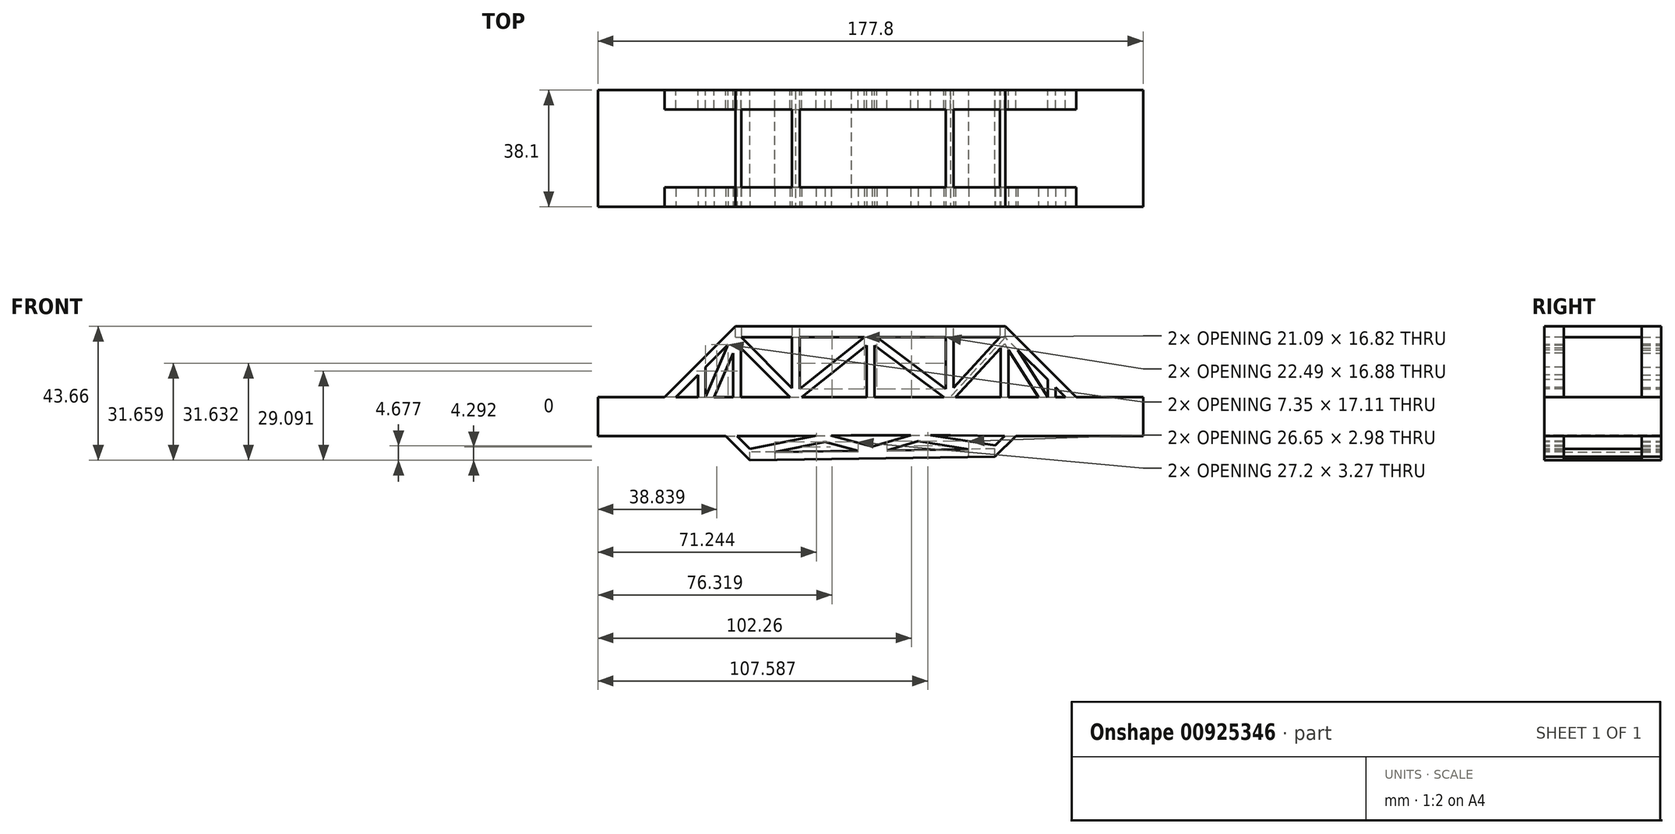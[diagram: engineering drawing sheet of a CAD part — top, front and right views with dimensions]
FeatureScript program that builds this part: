
annotation { "Feature Type Name" : "Feature", "Feature Type Description" : "" }
export const myFeature = defineFeature(function(context is Context, id is Id, definition is map)
    precondition{}
    {
        {
            var Q0;
            Q0=qCreatedBy(makeId("Front.planeOp"),FACE);
            var sketch = newSketch(context, id + "F0", { "sketchPlane" : qUnion([Q0])});
            skLineSegment(sketch, "E0.bottom", {"start": v(-75.3, -1.44) * mm, "end": v(51.7, -1.44) * mm});
            skLineSegment(sketch, "E1.bottom", {"start": v(-75.3, -1.44) * mm, "end": v(-100.7, -1.44) * mm});
            skLineSegment(sketch, "E1.top", {"start": v(-75.3, -14.14) * mm, "end": v(-100.7, -14.14) * mm});
            skLineSegment(sketch, "E1.left", {"start": v(-75.3, -8.45) * mm, "end": v(-75.3, -14.14) * mm});
            skLineSegment(sketch, "E1.right", {"start": v(-100.7, -1.44) * mm, "end": v(-100.7, -14.14) * mm});
            skPoint(sketch, "E2.oppositeSnap0", {"position": v(-88, -14.14) * mm});
            skLineSegment(sketch, "E2.bottom", {"start": v(51.7, -1.44) * mm, "end": v(77.1, -1.44) * mm});
            skLineSegment(sketch, "E2.left", {"start": v(51.7, -1.44) * mm, "end": v(51.7, -13.25) * mm});
            skLineSegment(sketch, "E2.right", {"start": v(77.1, -1.44) * mm, "end": v(77.1, -14.14) * mm});
            skPoint(sketch, "E3", {"position": v(-3.25, -27.46) * mm});
            skPoint(sketch, "E4", {"position": v(-50.06, -19.42) * mm});
            skPoint(sketch, "E5", {"position": v(27.7, -18.29) * mm});
            skPoint(sketch, "E6", {"position": v(-11.78, -13.8) * mm});
            skPoint(sketch, "E7", {"position": v(-36.3, -14.14) * mm});
            skPoint(sketch, "E8", {"position": v(37.87, -8.17) * mm});
            skLineSegment(sketch, "E9", {"start": v(-36.3, -14.14) * mm, "end": v(-36.3, -1.44) * mm});
            skLineSegment(sketch, "E10", {"start": v(-11.78, -13.8) * mm, "end": v(-11.78, -1.44) * mm});
            skLineSegment(sketch, "E11", {"start": v(-75.3, -1.44) * mm, "end": v(-75.3, -1.44) * mm});
            skLineSegment(sketch, "E12", {"start": v(-75.3, -8.45) * mm, "end": v(-75.3, -1.44) * mm});
            skLineSegment(sketch, "E13", {"start": v(51.7, -1.44) * mm, "end": v(32.16, 18.1) * mm});
            skLineSegment(sketch, "E14", {"start": v(32.16, 18.1) * mm, "end": v(-55.77, 18.1) * mm});
            skLineSegment(sketch, "E15", {"start": v(-55.77, 18.1) * mm, "end": v(-75.3, -1.44) * mm});
            skLineSegment(sketch, "E16", {"start": v(-65.53, 8.33) * mm, "end": v(-65.53, -1.44) * mm});
            skLineSegment(sketch, "E17", {"start": v(-64.15, -1.44) * mm, "end": v(-55.77, 18.1) * mm});
            skLineSegment(sketch, "E18", {"start": v(46.02, 4.24) * mm, "end": v(46.02, -1.44) * mm});
            skLineSegment(sketch, "E19", {"start": v(32.16, 18.1) * mm, "end": v(14.23, -1.44) * mm});
            skLineSegment(sketch, "E20", {"start": v(-11.8, 18.1) * mm, "end": v(14.23, -1.44) * mm});
            skLineSegment(sketch, "E21", {"start": v(-36.3, -1.44) * mm, "end": v(-11.8, 18.1) * mm});
            skLineSegment(sketch, "E22", {"start": v(-55.77, 18.1) * mm, "end": v(-36.3, -1.44) * mm});
            skLineSegment(sketch, "E23.1", {"start": v(31.98, 16.02) * mm, "end": v(15.96, -1.44) * mm});
            skLineSegment(sketch, "E23.2", {"start": v(-62.77, -1.44) * mm, "end": v(-55.34, 15.87) * mm});
            skLineSegment(sketch, "E23.3", {"start": v(-55.34, 15.87) * mm, "end": v(-38.08, -1.44) * mm});
            skLineSegment(sketch, "E23.4", {"start": v(-34.25, -1.44) * mm, "end": v(-11.78, 16.5) * mm});
            skLineSegment(sketch, "E23.5", {"start": v(-11.78, 16.5) * mm, "end": v(12.12, -1.44) * mm});
            skLineSegment(sketch, "E24.0", {"start": v(30.44, 18.1) * mm, "end": v(14.07, 0.27) * mm});
            skLineSegment(sketch, "E24.1", {"start": v(-9.69, 18.1) * mm, "end": v(14.07, 0.27) * mm});
            skLineSegment(sketch, "E24.2", {"start": v(-36.2, 0.27) * mm, "end": v(-13.84, 18.1) * mm});
            skLineSegment(sketch, "E24.3", {"start": v(-53.97, 18.1) * mm, "end": v(-36.2, 0.27) * mm});
            skLineSegment(sketch, "E25.0", {"start": v(-55.77, 21.7) * mm, "end": v(-78.9, -1.44) * mm});
            skLineSegment(sketch, "E26", {"start": v(-55.77, 21.7) * mm, "end": v(32.16, 21.7) * mm});
            skLineSegment(sketch, "E27.0", {"start": v(55.3, -1.44) * mm, "end": v(32.16, 21.7) * mm});
            skLineSegment(sketch, "E28", {"start": v(-55.34, -1.44) * mm, "end": v(-55.34, 15.87) * mm});
            skLineSegment(sketch, "E29", {"start": v(31.98, 16.02) * mm, "end": v(31.98, -1.44) * mm});
            skLineSegment(sketch, "E30", {"start": v(-11.78, 16.5) * mm, "end": v(-11.78, -1.44) * mm});
            skLineSegment(sketch, "E31", {"start": v(-36.2, 0.27) * mm, "end": v(-36.2, 18.1) * mm});
            skLineSegment(sketch, "E32", {"start": v(14.07, 0.27) * mm, "end": v(14.07, 18.1) * mm});
            skLineSegment(sketch, "E33.0", {"start": v(-34.92, 1.28) * mm, "end": v(-34.92, 18.1) * mm});
            skLineSegment(sketch, "E34.0", {"start": v(-37.46, 1.54) * mm, "end": v(-37.46, 18.1) * mm});
            skLineSegment(sketch, "E35.0", {"start": v(15.34, 1.65) * mm, "end": v(15.34, 18.1) * mm});
            skLineSegment(sketch, "E36.0", {"start": v(12.8, 1.22) * mm, "end": v(12.8, 18.1) * mm});
            skLineSegment(sketch, "E37.0", {"start": v(-54.07, -1.44) * mm, "end": v(-54.07, 14.6) * mm});
            skLineSegment(sketch, "E38.0", {"start": v(-56.61, -1.44) * mm, "end": v(-56.61, 12.91) * mm});
            skLineSegment(sketch, "E39.0", {"start": v(30.7, 14.63) * mm, "end": v(30.7, -1.44) * mm});
            skLineSegment(sketch, "E40.0", {"start": v(33.25, 14.01) * mm, "end": v(33.25, -1.44) * mm});
            skLineSegment(sketch, "E41", {"start": v(-37.46, 18.1) * mm, "end": v(-34.92, 18.1) * mm});
            skLineSegment(sketch, "E42", {"start": v(-37.46, 1.54) * mm, "end": v(-36.2, 0.27) * mm});
            skLineSegment(sketch, "E43", {"start": v(-36.2, 0.27) * mm, "end": v(-34.92, 1.28) * mm});
            skLineSegment(sketch, "E44.0", {"start": v(-13.05, 15.48) * mm, "end": v(-13.05, -1.44) * mm});
            skLineSegment(sketch, "E45.0", {"start": v(-10.5, 15.54) * mm, "end": v(-10.5, -1.44) * mm});
            skLineSegment(sketch, "E46.0", {"start": v(-68.07, 5.8) * mm, "end": v(-68.07, -1.44) * mm});
            skLineSegment(sketch, "E47", {"start": v(-18.13, -13.87) * mm, "end": v(-18.13, -1.44) * mm});
            skLineSegment(sketch, "E48", {"start": v(-5.43, -13.87) * mm, "end": v(-5.43, -1.44) * mm});
            skLineSegment(sketch, "E49.0", {"start": v(-65.53, -1.44) * mm, "end": v(-58.19, 15.68) * mm});
            skLineSegment(sketch, "E50", {"start": v(-55.34, -1.44) * mm, "end": v(-55.34, -14.14) * mm});
            skLineSegment(sketch, "E51", {"start": v(14.23, -1.44) * mm, "end": v(14.23, -13.87) * mm});
            skLineSegment(sketch, "E52", {"start": v(31.98, -1.44) * mm, "end": v(31.98, -14.14) * mm});
            skLineSegment(sketch, "E53", {"start": v(31.98, -14.14) * mm, "end": v(27.7, -18.29) * mm});
            skLineSegment(sketch, "E54", {"start": v(-50.06, -19.42) * mm, "end": v(27.7, -18.29) * mm});
            skLineSegment(sketch, "E55", {"start": v(-55.34, -14.14) * mm, "end": v(-50.06, -19.42) * mm});
            skPoint(sketch, "E56", {"position": v(3.63, -14.5) * mm});
            skPoint(sketch, "E57", {"position": v(-26.6, -14.74) * mm});
            skLineSegment(sketch, "E58", {"start": v(-75.3, -14.14) * mm, "end": v(-36.3, -14.14) * mm});
            skLineSegment(sketch, "E59", {"start": v(31.98, -14.14) * mm, "end": v(77.1, -14.14) * mm});
            skLineSegment(sketch, "E60.0", {"start": v(35.62, -14.14) * mm, "end": v(28.75, -20.81) * mm});
            skLineSegment(sketch, "E60.1", {"start": v(-51.1, -21.97) * mm, "end": v(28.75, -20.81) * mm});
            skLineSegment(sketch, "E60.2", {"start": v(-58.93, -14.14) * mm, "end": v(-51.1, -21.97) * mm});
            skLineSegment(sketch, "E61", {"start": v(27.7, -18.29) * mm, "end": v(3.63, -14.5) * mm});
            skLineSegment(sketch, "E62", {"start": v(3.63, -14.5) * mm, "end": v(-11.18, -18.85) * mm});
            skLineSegment(sketch, "E63", {"start": v(-11.18, -18.85) * mm, "end": v(-26.6, -14.74) * mm});
            skLineSegment(sketch, "E64", {"start": v(-26.6, -14.74) * mm, "end": v(-50.06, -19.42) * mm});
            skLineSegment(sketch, "E65.0", {"start": v(-29.59, -14.04) * mm, "end": v(-51.14, -18.34) * mm});
            skLineSegment(sketch, "E65.1", {"start": v(-11.2, -17.53) * mm, "end": v(-24.58, -13.97) * mm});
            skLineSegment(sketch, "E65.2", {"start": v(1.27, -13.87) * mm, "end": v(-11.2, -17.53) * mm});
            skLineSegment(sketch, "E65.3", {"start": v(28.84, -17.18) * mm, "end": v(7.78, -13.87) * mm});
            skLineSegment(sketch, "E66.0", {"start": v(-26.65, -16.04) * mm, "end": v(-43.06, -19.31) * mm});
            skLineSegment(sketch, "E66.1", {"start": v(-15.86, -18.92) * mm, "end": v(-26.65, -16.04) * mm});
            skLineSegment(sketch, "E66.2", {"start": v(3.71, -15.8) * mm, "end": v(-6.44, -18.78) * mm});
            skLineSegment(sketch, "E66.3", {"start": v(20.21, -18.4) * mm, "end": v(3.71, -15.8) * mm});
            skLineSegment(sketch, "E67", {"start": v(-5.43, -13.87) * mm, "end": v(14.23, -13.87) * mm});
            skLineSegment(sketch, "E68", {"start": v(-5.43, -13.87) * mm, "end": v(-18.13, -13.87) * mm});
            skLineSegment(sketch, "E69", {"start": v(-36.3, -14.14) * mm, "end": v(-18.13, -13.87) * mm});
            skLineSegment(sketch, "E70", {"start": v(-11.78, -13.8) * mm, "end": v(-11.18, -18.85) * mm, "construction": true});
            skLineSegment(sketch, "E71", {"start": v(14.23, -13.87) * mm, "end": v(31.98, -14.14) * mm});
            skLineSegment(sketch, "E72", {"start": v(48.56, 1.7) * mm, "end": v(48.56, -1.44) * mm});
            skLineSegment(sketch, "E73", {"start": v(31.98, 16.02) * mm, "end": v(43.02, -1.44) * mm});
            skLineSegment(sketch, "E74", {"start": v(46.02, -1.44) * mm, "end": v(36.25, 14.01) * mm});
            skLineSegment(sketch, "E75", {"start": v(32.16, 18.1) * mm, "end": v(44.52, -1.44) * mm});
            skSolve(sketch);
        }
        {
            var Q0;
            Q0=makeQuery(id+"F0.imprint","IMPRINT",FACE,{"disambiguationData":[TD([[makeQuery(id+"F0.imprint","IMPRINT",EDGE,{"derivedFrom":sQuery(id+"F0.wireOp",EDGE,"E1.top")}),-1.0]])]});
            var Q1;
            {var subQ11=sQuery(id+"F0.wireOp",EDGE,"E2.right");Q1=makeQuery(id+"F0.imprint","IMPRINT",FACE,{"disambiguationData":[TD([[makeQuery(id+"F0.imprint","IMPRINT",EDGE,{"derivedFrom":subQ11}),-1.0]])]});}
            extrude(context, id + "F1", {"entities" : qUnion([Q0, Q1]), "oppositeDirection" : true, "depth" : 19.05 * mm, "offsetDistance" : 25.4 * mm});
        }
        {
            var Q0;
            {var subQ8=sQuery(id+"F0.wireOp",EDGE,"E1.left");Q0=makeQuery(id+"F0.imprint","IMPRINT",FACE,{"disambiguationData":[TD([[makeQuery(id+"F0.imprint","IMPRINT",EDGE,{"derivedFrom":subQ8}),1.0]])]});}
            var Q1;
            {var subQ0=sQuery(id+"F0.wireOp",EDGE,"E9");Q1=makeQuery(id+"F0.imprint","IMPRINT",FACE,{"disambiguationData":[TD([[makeQuery(id+"F0.imprint","IMPRINT",EDGE,{"derivedFrom":subQ0}),1.0]])]});}
            var Q2;
            {var subQ4=sQuery(id+"F0.wireOp",EDGE,"E48");Q2=makeQuery(id+"F0.imprint","IMPRINT",FACE,{"disambiguationData":[TD([[makeQuery(id+"F0.imprint","IMPRINT",EDGE,{"derivedFrom":subQ4}),-1.0]])]});}
            var Q3;
            {var subQ0=sQuery(id+"F0.wireOp",EDGE,"E51");Q3=makeQuery(id+"F0.imprint","IMPRINT",FACE,{"disambiguationData":[TD([[makeQuery(id+"F0.imprint","IMPRINT",EDGE,{"derivedFrom":subQ0}),1.0]])]});}
            var Q4;
            {var subQ4=sQuery(id+"F0.wireOp",EDGE,"E2.left");Q4=makeQuery(id+"F0.imprint","IMPRINT",FACE,{"disambiguationData":[TD([[makeQuery(id+"F0.imprint","IMPRINT",EDGE,{"derivedFrom":subQ4}),-1.0]])]});}
            var Q5;
            {var subQ1=sQuery(id+"F0.wireOp",EDGE,"E9");Q5=makeQuery(id+"F0.imprint","IMPRINT",FACE,{"disambiguationData":[TD([[makeQuery(id+"F0.imprint","IMPRINT",EDGE,{"derivedFrom":subQ1}),-1.0]])]});}
            extrude(context, id + "F2", {"entities" : qUnion([Q0, Q1, Q2, Q3, Q4, Q5]), "operationType" : NewBodyOperationType.ADD, "oppositeDirection" : true, "depth" : 19.05 * mm, "offsetDistance" : 25.4 * mm});
        }
        {
            var Q0;
            Q0=makeQuery(id+"F2.opExtrude","SWEPT_FACE",FACE,{"disambiguationData":[OSD([sQuery(id+"F0.wireOp",EDGE,"E48")])]});
            extrude(context, id + "F3", {"entities" : qUnion([Q0]), "operationType" : NewBodyOperationType.ADD, "endBound" : BoundingType.UP_TO_NEXT, "depth" : 25.4 * mm, "offsetDistance" : 25.4 * mm});
        }
        {
            var Q0;
            {var subQ27=sQuery(id+"F0.wireOp",EDGE,"E25.0");Q0=makeQuery(id+"F0.imprint","IMPRINT",FACE,{"disambiguationData":[TD([[makeQuery(id+"F0.imprint","IMPRINT",EDGE,{"derivedFrom":subQ27}),1.0]])]});}
            var Q1;
            {var subQ0=sQuery(id+"F0.wireOp",EDGE,"E16");Q1=makeQuery(id+"F0.imprint","IMPRINT",FACE,{"disambiguationData":[TD([[makeQuery(id+"F0.imprint","IMPRINT",EDGE,{"derivedFrom":subQ0}),-1.0]])]});}
            var Q2;
            {var subQ0=sQuery(id+"F0.wireOp",EDGE,"E31");Q2=makeQuery(id+"F0.imprint","IMPRINT",FACE,{"disambiguationData":[TD([[makeQuery(id+"F0.imprint","IMPRINT",EDGE,{"derivedFrom":subQ0}),1.0]])]});}
            var Q3;
            {var subQ0=sQuery(id+"F0.wireOp",EDGE,"E31");Q3=makeQuery(id+"F0.imprint","IMPRINT",FACE,{"disambiguationData":[TD([[makeQuery(id+"F0.imprint","IMPRINT",EDGE,{"derivedFrom":subQ0}),-1.0]])]});}
            var Q4;
            {var subQ0=sQuery(id+"F0.wireOp",EDGE,"E30");Q4=makeQuery(id+"F0.imprint","IMPRINT",FACE,{"disambiguationData":[TD([[makeQuery(id+"F0.imprint","IMPRINT",EDGE,{"derivedFrom":subQ0}),-1.0]])]});}
            var Q5;
            {var subQ0=sQuery(id+"F0.wireOp",EDGE,"E30");Q5=makeQuery(id+"F0.imprint","IMPRINT",FACE,{"disambiguationData":[TD([[makeQuery(id+"F0.imprint","IMPRINT",EDGE,{"derivedFrom":subQ0}),1.0]])]});}
            var Q6;
            {var subQ0=sQuery(id+"F0.wireOp",EDGE,"E32");Q6=makeQuery(id+"F0.imprint","IMPRINT",FACE,{"disambiguationData":[TD([[makeQuery(id+"F0.imprint","IMPRINT",EDGE,{"derivedFrom":subQ0}),-1.0]])]});}
            var Q7;
            {var subQ2=sQuery(id+"F0.wireOp",EDGE,"E32");Q7=makeQuery(id+"F0.imprint","IMPRINT",FACE,{"disambiguationData":[TD([[makeQuery(id+"F0.imprint","IMPRINT",EDGE,{"derivedFrom":subQ2}),1.0]])]});}
            var Q8;
            {var subQ0=sQuery(id+"F0.wireOp",EDGE,"E29");Q8=makeQuery(id+"F0.imprint","IMPRINT",FACE,{"disambiguationData":[TD([[makeQuery(id+"F0.imprint","IMPRINT",EDGE,{"derivedFrom":subQ0}),-1.0]])]});}
            var Q9;
            {var subQ0=sQuery(id+"F0.wireOp",EDGE,"E29");Q9=makeQuery(id+"F0.imprint","IMPRINT",FACE,{"disambiguationData":[TD([[makeQuery(id+"F0.imprint","IMPRINT",EDGE,{"derivedFrom":subQ0}),1.0]])]});}
            var Q10;
            {var subQ0=sQuery(id+"F0.wireOp",EDGE,"E28");Q10=makeQuery(id+"F0.imprint","IMPRINT",FACE,{"disambiguationData":[TD([[makeQuery(id+"F0.imprint","IMPRINT",EDGE,{"derivedFrom":subQ0}),-1.0]])]});}
            var Q11;
            {var subQ0=sQuery(id+"F0.wireOp",EDGE,"E28");Q11=makeQuery(id+"F0.imprint","IMPRINT",FACE,{"disambiguationData":[TD([[makeQuery(id+"F0.imprint","IMPRINT",EDGE,{"derivedFrom":subQ0}),1.0]])]});}
            var Q12;
            {var subQ0=sQuery(id+"F0.wireOp",EDGE,"E48");var subQ1=sQuery(id+"F0.wireOp",EDGE,"E12");var subQ2=sQuery(id+"F0.wireOp",EDGE,"E1.left");var subQ3=sQuery(id+"F0.wireOp",EDGE,"E0.bottom");var subQ4=sQuery(id+"F0.wireOp",EDGE,"E52");Q12=makeQuery(id+"F3.boolean.opBoolean","MERGE",FACE,{"derivedFrom":[makeQuery(id+"F2.boolean.opBoolean","MERGE",FACE,{"derivedFrom":[makeQuery(id+"F1.opExtrude","CAP_FACE",FACE,{"disambiguationData":[OSD([subQ3,sQuery(id+"F0.wireOp",EDGE,"E2.bottom"),sQuery(id+"F0.wireOp",EDGE,"E2.right"),subQ4,sQuery(id+"F0.wireOp",EDGE,"E59")])],"isStart":false}),makeQuery(id+"F2.opExtrude","CAP_FACE",FACE,{"disambiguationData":[OSD([subQ3,subQ0,subQ4,sQuery(id+"F0.wireOp",EDGE,"E67"),sQuery(id+"F0.wireOp",EDGE,"E71")])],"isStart":false})]}),makeQuery(id+"F2.boolean.opBoolean","MERGE",FACE,{"derivedFrom":[makeQuery(id+"F1.opExtrude","CAP_FACE",FACE,{"disambiguationData":[OSD([sQuery(id+"F0.wireOp",EDGE,"E1.bottom"),sQuery(id+"F0.wireOp",EDGE,"E1.top"),subQ2,sQuery(id+"F0.wireOp",EDGE,"E1.right"),subQ1])],"isStart":false}),makeQuery(id+"F2.opExtrude","CAP_FACE",FACE,{"disambiguationData":[OSD([subQ3,subQ2,subQ1,sQuery(id+"F0.wireOp",EDGE,"E47"),sQuery(id+"F0.wireOp",EDGE,"E58"),sQuery(id+"F0.wireOp",EDGE,"E69")])],"isStart":false})]}),makeQuery(id+"F3.opExtrude","SWEPT_FACE",FACE,{"disambiguationData":[OSD([subQ0]),TDD([makeQuery(id+"F2.opExtrude","CAP_EDGE",EDGE,{"disambiguationData":[OSD([subQ0])],"isStart":false})])]})]});}
            extrude(context, id + "F4", {"entities" : qUnion([Q0, Q1, Q2, Q3, Q4, Q5, Q6, Q7, Q8, Q9, Q10, Q11]), "operationType" : NewBodyOperationType.ADD, "oppositeDirection" : true, "depth" : 6.35 * mm, "endBoundEntityFace" : qUnion([Q12]), "offsetDistance" : 25.4 * mm});
        }
        {
            var Q0;
            {var subQ1=sQuery(id+"F0.wireOp",EDGE,"E17");Q0=makeQuery(id+"F0.imprint","IMPRINT",FACE,{"disambiguationData":[TD([[makeQuery(id+"F0.imprint","IMPRINT",EDGE,{"derivedFrom":subQ1}),-1.0]])]});}
            var Q1;
            {var subQ2=sQuery(id+"F0.wireOp",EDGE,"E17");Q1=makeQuery(id+"F0.imprint","IMPRINT",FACE,{"disambiguationData":[TD([[makeQuery(id+"F0.imprint","IMPRINT",EDGE,{"derivedFrom":subQ2}),1.0]])]});}
            var Q2;
            {var subQ1=sQuery(id+"F0.wireOp",EDGE,"E21");Q2=makeQuery(id+"F0.imprint","IMPRINT",FACE,{"disambiguationData":[TD([[makeQuery(id+"F0.imprint","IMPRINT",EDGE,{"derivedFrom":subQ1}),1.0]])]});}
            var Q3;
            {var subQ5=sQuery(id+"F0.wireOp",EDGE,"E20");Q3=makeQuery(id+"F0.imprint","IMPRINT",FACE,{"disambiguationData":[TD([[makeQuery(id+"F0.imprint","IMPRINT",EDGE,{"derivedFrom":subQ5}),-1.0]])]});}
            var Q4;
            {var subQ1=sQuery(id+"F0.wireOp",EDGE,"E19");Q4=makeQuery(id+"F0.imprint","IMPRINT",FACE,{"disambiguationData":[TD([[makeQuery(id+"F0.imprint","IMPRINT",EDGE,{"derivedFrom":subQ1}),-1.0]])]});}
            var Q5;
            {var subQ4=sQuery(id+"F0.wireOp",EDGE,"FBquyQBi-Z4om-dfKi-FxFz-UrPSVaUbQBql");Q5=makeQuery(id+"F0.imprint","IMPRINT",FACE,{"disambiguationData":[TD([[makeQuery(id+"F0.imprint","IMPRINT",EDGE,{"derivedFrom":subQ4}),-1.0]])]});}
            extrude(context, id + "F5", {"entities" : qUnion([Q0, Q1, Q2, Q3, Q4, Q5]), "operationType" : NewBodyOperationType.ADD, "oppositeDirection" : true, "depth" : 6.35 * mm, "offsetDistance" : 25.4 * mm});
        }
        {
            var Q0;
            {var subQ27=sQuery(id+"F0.wireOp",EDGE,"E25.0");Q0=makeQuery(id+"F0.imprint","IMPRINT",FACE,{"disambiguationData":[TD([[makeQuery(id+"F0.imprint","IMPRINT",EDGE,{"derivedFrom":subQ27}),1.0]])]});}
            var sketch = newSketch(context, id + "F6", { "sketchPlane" : qUnion([Q0])});
            skLineSegment(sketch, "E76.bottom", {"start": v(32.16, 21.7) * mm, "end": v(30.44, 21.7) * mm});
            skLineSegment(sketch, "E76.top", {"start": v(32.16, 18.1) * mm, "end": v(30.44, 18.1) * mm});
            skLineSegment(sketch, "E76.left", {"start": v(32.16, 21.7) * mm, "end": v(32.16, 18.1) * mm});
            skLineSegment(sketch, "E76.right", {"start": v(30.44, 21.7) * mm, "end": v(30.44, 18.1) * mm});
            skLineSegment(sketch, "E77.bottom", {"start": v(15.34, 18.1) * mm, "end": v(12.8, 18.1) * mm});
            skLineSegment(sketch, "E77.top", {"start": v(15.34, 21.7) * mm, "end": v(12.8, 21.7) * mm});
            skLineSegment(sketch, "E77.left", {"start": v(15.34, 18.1) * mm, "end": v(15.34, 21.7) * mm});
            skLineSegment(sketch, "E77.right", {"start": v(12.8, 18.1) * mm, "end": v(12.8, 21.7) * mm});
            skLineSegment(sketch, "E78.bottom", {"start": v(-9.69, 21.7) * mm, "end": v(-13.84, 21.7) * mm});
            skLineSegment(sketch, "E78.top", {"start": v(-9.69, 18.1) * mm, "end": v(-13.84, 18.1) * mm});
            skLineSegment(sketch, "E78.left", {"start": v(-9.69, 21.7) * mm, "end": v(-9.69, 18.1) * mm});
            skLineSegment(sketch, "E78.right", {"start": v(-13.84, 21.7) * mm, "end": v(-13.84, 18.1) * mm});
            skLineSegment(sketch, "E79.bottom", {"start": v(-34.92, 21.7) * mm, "end": v(-37.46, 21.7) * mm});
            skLineSegment(sketch, "E79.top", {"start": v(-34.92, 18.1) * mm, "end": v(-37.46, 18.1) * mm});
            skLineSegment(sketch, "E79.left", {"start": v(-34.92, 21.7) * mm, "end": v(-34.92, 18.1) * mm});
            skLineSegment(sketch, "E79.right", {"start": v(-37.46, 21.7) * mm, "end": v(-37.46, 18.1) * mm});
            skLineSegment(sketch, "E80.bottom", {"start": v(-53.97, 21.7) * mm, "end": v(-55.77, 21.7) * mm});
            skLineSegment(sketch, "E80.top", {"start": v(-53.97, 18.1) * mm, "end": v(-55.77, 18.1) * mm});
            skLineSegment(sketch, "E80.left", {"start": v(-53.97, 21.7) * mm, "end": v(-53.97, 18.1) * mm});
            skLineSegment(sketch, "E80.right", {"start": v(-55.77, 21.7) * mm, "end": v(-55.77, 18.1) * mm});
            skSolve(sketch);
        }
        {
            var Q0;
            {var subQ17=sQuery(id+"F0.wireOp",EDGE,"E60.0");Q0=makeQuery(id+"F0.imprint","IMPRINT",FACE,{"disambiguationData":[TD([[makeQuery(id+"F0.imprint","IMPRINT",EDGE,{"derivedFrom":subQ17}),-1.0]])]});}
            var Q1;
            {var subQ1=sQuery(id+"F0.wireOp",EDGE,"E63");Q1=makeQuery(id+"F0.imprint","IMPRINT",FACE,{"disambiguationData":[TD([[makeQuery(id+"F0.imprint","IMPRINT",EDGE,{"derivedFrom":subQ1}),1.0]])]});}
            var Q2;
            {var subQ2=sQuery(id+"F0.wireOp",EDGE,"E61");Q2=makeQuery(id+"F0.imprint","IMPRINT",FACE,{"disambiguationData":[TD([[makeQuery(id+"F0.imprint","IMPRINT",EDGE,{"derivedFrom":subQ2}),-1.0]])]});}
            var Q3;
            {var subQ0=sQuery(id+"F0.wireOp",EDGE,"E61");Q3=makeQuery(id+"F0.imprint","IMPRINT",FACE,{"disambiguationData":[TD([[makeQuery(id+"F0.imprint","IMPRINT",EDGE,{"derivedFrom":subQ0}),1.0]])]});}
            extrude(context, id + "F7", {"entities" : qUnion([Q0, Q1, Q2, Q3]), "operationType" : NewBodyOperationType.ADD, "oppositeDirection" : true, "depth" : 6.35 * mm, "offsetDistance" : 25.4 * mm});
        }
        {
            var Q0;
            {var subQ2=sQuery(id+"F0.wireOp",EDGE,"FBquyQBi-Z4om-dfKi-FxFz-UrPSVaUbQBql");Q0=makeQuery(id+"F0.imprint","IMPRINT",FACE,{"disambiguationData":[TD([[makeQuery(id+"F0.imprint","IMPRINT",EDGE,{"derivedFrom":subQ2}),1.0]])]});}
            var Q1;
            {var subQ0=sQuery(id+"F0.wireOp",EDGE,"E18");Q1=makeQuery(id+"F0.imprint","IMPRINT",FACE,{"disambiguationData":[TD([[makeQuery(id+"F0.imprint","IMPRINT",EDGE,{"derivedFrom":subQ0}),1.0]])]});}
            extrude(context, id + "F8", {"entities" : qUnion([Q0, Q1]), "operationType" : NewBodyOperationType.ADD, "oppositeDirection" : true, "depth" : 6.35 * mm, "offsetDistance" : 25.4 * mm});
        }
        {
            var Q0;
            Q0=makeQuery(id+"F1.opExtrude","SWEPT_BODY",BODY,{"disambiguationData":[OSD([sQuery(id+"F0.wireOp",EDGE,"E0.bottom"),sQuery(id+"F0.wireOp",EDGE,"E2.bottom"),sQuery(id+"F0.wireOp",EDGE,"E2.right"),sQuery(id+"F0.wireOp",EDGE,"E52"),sQuery(id+"F0.wireOp",EDGE,"E59")])]});
            var Q1;
            {var subQ0=sQuery(id+"F0.wireOp",EDGE,"E48");var subQ1=sQuery(id+"F0.wireOp",EDGE,"E12");var subQ2=sQuery(id+"F0.wireOp",EDGE,"E1.left");var subQ3=sQuery(id+"F0.wireOp",EDGE,"E0.bottom");var subQ4=sQuery(id+"F0.wireOp",EDGE,"E52");Q1=makeQuery(id+"F3.boolean.opBoolean","MERGE",FACE,{"derivedFrom":[makeQuery(id+"F2.boolean.opBoolean","MERGE",FACE,{"derivedFrom":[makeQuery(id+"F1.opExtrude","CAP_FACE",FACE,{"disambiguationData":[OSD([subQ3,sQuery(id+"F0.wireOp",EDGE,"E2.bottom"),sQuery(id+"F0.wireOp",EDGE,"E2.right"),subQ4,sQuery(id+"F0.wireOp",EDGE,"E59")])],"isStart":false}),makeQuery(id+"F2.opExtrude","CAP_FACE",FACE,{"disambiguationData":[OSD([subQ3,subQ0,subQ4,sQuery(id+"F0.wireOp",EDGE,"E67"),sQuery(id+"F0.wireOp",EDGE,"E71")])],"isStart":false})]}),makeQuery(id+"F2.boolean.opBoolean","MERGE",FACE,{"derivedFrom":[makeQuery(id+"F1.opExtrude","CAP_FACE",FACE,{"disambiguationData":[OSD([sQuery(id+"F0.wireOp",EDGE,"E1.bottom"),sQuery(id+"F0.wireOp",EDGE,"E1.top"),subQ2,sQuery(id+"F0.wireOp",EDGE,"E1.right"),subQ1])],"isStart":false}),makeQuery(id+"F2.opExtrude","CAP_FACE",FACE,{"disambiguationData":[OSD([subQ3,subQ2,subQ1,sQuery(id+"F0.wireOp",EDGE,"E47"),sQuery(id+"F0.wireOp",EDGE,"E58"),sQuery(id+"F0.wireOp",EDGE,"E69")])],"isStart":false})]}),makeQuery(id+"F3.opExtrude","SWEPT_FACE",FACE,{"disambiguationData":[OSD([subQ0]),TDD([makeQuery(id+"F2.opExtrude","CAP_EDGE",EDGE,{"disambiguationData":[OSD([subQ0])],"isStart":false})])]})]});}
            mirror(context, id + "F9", {"operationType" : NewBodyOperationType.ADD, "entities" : qUnion([Q0]), "mirrorPlane" : qUnion([Q1])});
        }
        {
            var Q0;
            {var subQ0=sQuery(id+"F0.wireOp",EDGE,"E13");var subQ1=sQuery(id+"F0.wireOp",EDGE,"E0.bottom");var subQ2=sQuery(id+"F0.wireOp",EDGE,"E24.3");var subQ3=sQuery(id+"F0.wireOp",EDGE,"E24.2");var subQ4=sQuery(id+"F0.wireOp",EDGE,"E24.1");var subQ5=sQuery(id+"F0.wireOp",EDGE,"E24.0");var subQ6=sQuery(id+"F0.wireOp",EDGE,"E23.5");var subQ7=sQuery(id+"F0.wireOp",EDGE,"E23.4");var subQ8=sQuery(id+"F0.wireOp",EDGE,"E23.3");var subQ9=sQuery(id+"F0.wireOp",EDGE,"E23.2");var subQ10=sQuery(id+"F0.wireOp",EDGE,"E15");var subQ11=sQuery(id+"F0.wireOp",EDGE,"E14");Q0=makeQuery(id+"F9.opPattern","COPY",FACE,{"derivedFrom":makeQuery(id+"F8.boolean.opBoolean","MERGE",FACE,{"derivedFrom":[makeQuery(id+"F5.boolean.opBoolean","MERGE",FACE,{"derivedFrom":[makeQuery(id+"F4.opExtrude","CAP_FACE",FACE,{"disambiguationData":[OSD([subQ1,sQuery(id+"F0.wireOp",EDGE,"E1.bottom"),sQuery(id+"F0.wireOp",EDGE,"E2.bottom"),subQ0,subQ11,subQ10,sQuery(id+"F0.wireOp",EDGE,"E16"),subQ5,subQ4,subQ3,subQ2,sQuery(id+"F0.wireOp",EDGE,"E25.0"),sQuery(id+"F0.wireOp",EDGE,"E26"),sQuery(id+"F0.wireOp",EDGE,"E27.0"),sQuery(id+"F0.wireOp",EDGE,"E33.0"),sQuery(id+"F0.wireOp",EDGE,"E34.0"),sQuery(id+"F0.wireOp",EDGE,"E35.0"),sQuery(id+"F0.wireOp",EDGE,"E36.0"),sQuery(id+"F0.wireOp",EDGE,"E46.0")])],"isStart":false}),makeQuery(id+"F4.opExtrude","CAP_FACE",FACE,{"disambiguationData":[OSD([subQ1,subQ9,subQ8,sQuery(id+"F0.wireOp",EDGE,"E37.0"),sQuery(id+"F0.wireOp",EDGE,"E38.0")])],"isStart":false}),makeQuery(id+"F4.opExtrude","CAP_FACE",FACE,{"disambiguationData":[OSD([subQ1,subQ7,subQ6,sQuery(id+"F0.wireOp",EDGE,"E44.0"),sQuery(id+"F0.wireOp",EDGE,"E45.0")])],"isStart":false}),makeQuery(id+"F5.opExtrude","CAP_FACE",FACE,{"disambiguationData":[OSD([subQ1,subQ11,subQ10,sQuery(id+"F0.wireOp",EDGE,"E19"),subQ9,subQ8,subQ7,subQ6,subQ5,subQ4,subQ3,subQ2,sQuery(id+"F0.wireOp",EDGE,"E49.0")])],"isStart":false})]}),makeQuery(id+"F8.opExtrude","CAP_FACE",FACE,{"disambiguationData":[OSD([subQ1,subQ0,sQuery(id+"F0.wireOp",EDGE,"E18"),sQuery(id+"F0.wireOp",EDGE,"E72")])],"isStart":false})]}),"instanceName":"1"});}
            var sketch = newSketch(context, id + "F10", { "sketchPlane" : qUnion([Q0])});
            skLineSegment(sketch, "E81.bottom", {"start": v(28.75, -20.81) * mm, "end": v(20.25, -20.94) * mm});
            skLineSegment(sketch, "E81.top", {"start": v(28.7, -18.27) * mm, "end": v(20.21, -18.4) * mm});
            skLineSegment(sketch, "E81.left", {"start": v(28.75, -20.81) * mm, "end": v(28.7, -18.27) * mm});
            skLineSegment(sketch, "E81.right", {"start": v(20.25, -20.94) * mm, "end": v(20.21, -18.4) * mm});
            skLineSegment(sketch, "E82.bottom", {"start": v(-51.1, -21.97) * mm, "end": v(-51.1, -21.97) * mm});
            skLineSegment(sketch, "E82.top", {"start": v(-43.06, -19.31) * mm, "end": v(-51.1, -19.31) * mm});
            skLineSegment(sketch, "E82.left", {"start": v(-51.1, -21.97) * mm, "end": v(-51.1, -19.33) * mm});
            skLineSegment(sketch, "E82.right", {"start": v(-51.1, -21.97) * mm, "end": v(-51.1, -19.31) * mm});
            skLineSegment(sketch, "E83", {"start": v(-43.06, -19.31) * mm, "end": v(-43.06, -21.85) * mm});
            skLineSegment(sketch, "E84", {"start": v(-43.06, -21.85) * mm, "end": v(-51.1, -21.97) * mm});
            skSolve(sketch);
        }
        {
            var Q0;
            Q0=makeQuery(id+"F10.imprint","IMPRINT",FACE,{"disambiguationData":[TD([[makeQuery(id+"F10.imprint","IMPRINT",EDGE,{"derivedFrom":sQuery(id+"F10.wireOp",EDGE,"E81.bottom")}),-1.0]])]});
            extrude(context, id + "F11", {"entities" : qUnion([Q0]), "operationType" : NewBodyOperationType.ADD, "endBound" : BoundingType.UP_TO_NEXT, "depth" : 25.4 * mm, "offsetDistance" : 25.4 * mm});
        }
        {
            var Q0;
            Q0=makeQuery(id+"F10.imprint","IMPRINT",FACE,{"disambiguationData":[TD([[makeQuery(id+"F10.imprint","IMPRINT",EDGE,{"derivedFrom":sQuery(id+"F10.wireOp",EDGE,"E82.top")}),1.0]])]});
            var Q1;
            Q1=makeQuery(id+"F7.opExtrude","CAP_FACE",FACE,{"disambiguationData":[OSD([sQuery(id+"F0.wireOp",EDGE,"E53"),sQuery(id+"F0.wireOp",EDGE,"E54"),sQuery(id+"F0.wireOp",EDGE,"E55"),sQuery(id+"F0.wireOp",EDGE,"E58"),sQuery(id+"F0.wireOp",EDGE,"E59"),sQuery(id+"F0.wireOp",EDGE,"E60.0"),sQuery(id+"F0.wireOp",EDGE,"E60.1"),sQuery(id+"F0.wireOp",EDGE,"E60.2"),sQuery(id+"F0.wireOp",EDGE,"E65.0"),sQuery(id+"F0.wireOp",EDGE,"E65.1"),sQuery(id+"F0.wireOp",EDGE,"E65.2"),sQuery(id+"F0.wireOp",EDGE,"E65.3"),sQuery(id+"F0.wireOp",EDGE,"E66.0"),sQuery(id+"F0.wireOp",EDGE,"E66.1"),sQuery(id+"F0.wireOp",EDGE,"E66.2"),sQuery(id+"F0.wireOp",EDGE,"E66.3"),sQuery(id+"F0.wireOp",EDGE,"E67"),sQuery(id+"F0.wireOp",EDGE,"E69")])],"isStart":false});
            var Q2;
            Q2=sQuery(id+"F0.wireOp",VERTEX,"E37.0.start");
            extrude(context, id + "F12", {"entities" : qUnion([Q0]), "operationType" : NewBodyOperationType.ADD, "endBound" : BoundingType.UP_TO_NEXT, "depth" : 25.4 * mm, "endBoundEntityFace" : qUnion([Q1]), "endBoundEntityVertex" : qUnion([Q2]), "offsetDistance" : 25.4 * mm});
        }
        {
            var Q0;
            Q0=makeQuery(id+"F6.imprint","IMPRINT",FACE,{"disambiguationData":[TD([[makeQuery(id+"F6.imprint","IMPRINT",EDGE,{"derivedFrom":sQuery(id+"F6.wireOp",EDGE,"E77.top")}),-1.0]])]});
            var Q1;
            Q1=makeQuery(id+"F6.imprint","IMPRINT",FACE,{"disambiguationData":[TD([[makeQuery(id+"F6.imprint","IMPRINT",EDGE,{"derivedFrom":sQuery(id+"F6.wireOp",EDGE,"E76.bottom")}),-1.0]])]});
            var Q2;
            Q2=makeQuery(id+"F6.imprint","IMPRINT",FACE,{"disambiguationData":[TD([[makeQuery(id+"F6.imprint","IMPRINT",EDGE,{"derivedFrom":sQuery(id+"F6.wireOp",EDGE,"E80.bottom")}),-1.0]])]});
            var Q3;
            Q3=makeQuery(id+"F6.imprint","IMPRINT",FACE,{"disambiguationData":[TD([[makeQuery(id+"F6.imprint","IMPRINT",EDGE,{"derivedFrom":sQuery(id+"F6.wireOp",EDGE,"E79.bottom")}),-1.0]])]});
            extrude(context, id + "F13", {"entities" : qUnion([Q0, Q1, Q2, Q3]), "operationType" : NewBodyOperationType.ADD, "oppositeDirection" : true, "depth" : 38.1 * mm, "offsetDistance" : 25.4 * mm});
        }
        {
            var Q0;
            {var subQ4=sQuery(id+"F0.wireOp",EDGE,"E19");Q0=makeQuery(id+"F0.imprint","IMPRINT",FACE,{"disambiguationData":[TD([[makeQuery(id+"F0.imprint","IMPRINT",EDGE,{"derivedFrom":subQ4}),1.0]])]});}
            var Q1;
            {var subQ0=sQuery(id+"F0.wireOp",EDGE,"E74");Q1=makeQuery(id+"F0.imprint","IMPRINT",FACE,{"disambiguationData":[TD([[makeQuery(id+"F0.imprint","IMPRINT",EDGE,{"derivedFrom":subQ0}),1.0]])]});}
            extrude(context, id + "F14", {"entities" : qUnion([Q0, Q1]), "operationType" : NewBodyOperationType.ADD, "oppositeDirection" : true, "depth" : 6.35 * mm, "offsetDistance" : 25.4 * mm});
        }
    });
